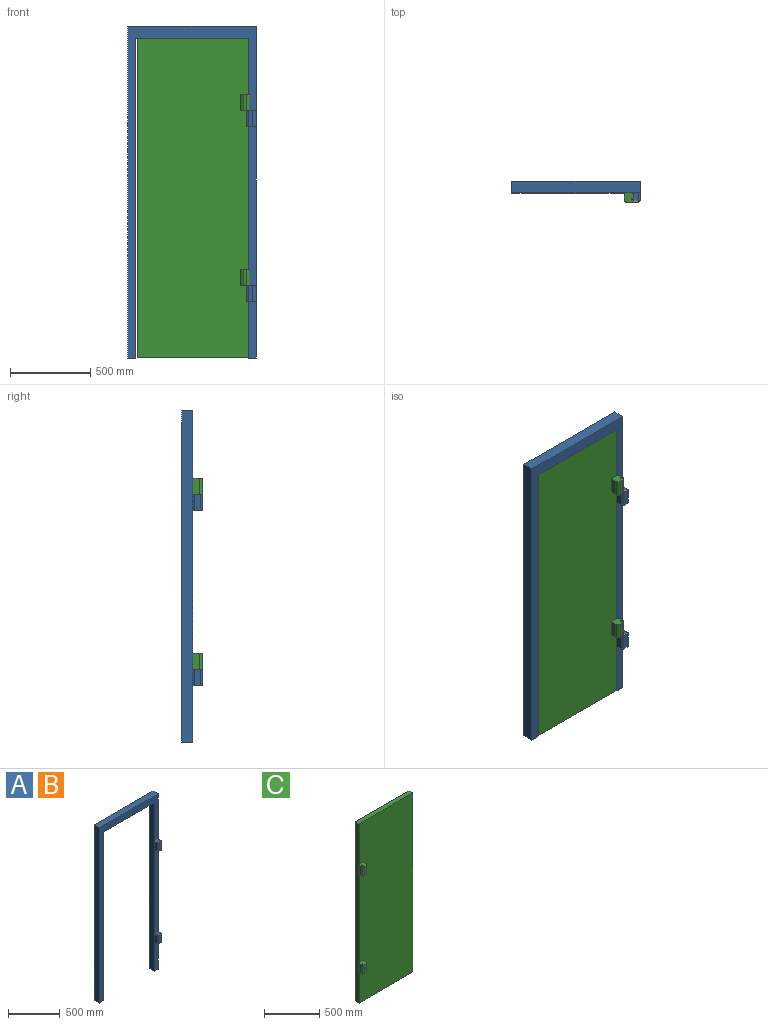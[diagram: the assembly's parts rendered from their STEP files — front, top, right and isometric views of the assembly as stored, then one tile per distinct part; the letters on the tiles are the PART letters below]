
ASSEMBLY  parts=3 mates=1
PART A: 32 faces, bbox 800x130x2070 mm
  f0: plane 2070x800mm, normal (0,-1,0), area 182944.4mm2, adj f2,f3,f4,f5,f6,f7,f9,f16
  f1: plane 1014.1x50mm, normal (0,-1,0), area 49748.1mm2, adj f7,f9,f12,f18,f21,f25
  f2: plane 800x70mm, normal (0,0,1), area 56000mm2, adj f0,f3,f9,f11
  f3: plane 2070x70mm, normal (-1,0,0), area 144900mm2, adj f0,f2,f4,f11
  f4: plane 70x50mm, normal (0,0,-1), area 3500mm2, adj f0,f3,f5,f11
  f5: plane 1994.1x70mm, normal (1,0,0), area 139587.2mm2, adj f0,f4,f6,f11
  f6: plane 700x70mm, normal (0,0,-1), area 49000mm2, adj f0,f5,f7,f11
  f7: plane 1994.1x70mm, normal (-1,0,0), area 139587.2mm2, adj f0,f1,f6,f8,f10,f11,f22,f26
  f8: plane 70x50mm, normal (0,0,-1), area 3500mm2, adj f7,f9,f10,f11
  f9: plane 2070x110mm, normal (1,0,0), area 151300mm2, adj f0,f1,f2,f8,f10,f11,f20,f21
  f10: plane 360x50mm, normal (0,-1,0), area 17521.5mm2, adj f7,f8,f9,f14,f20
  f11: plane 2070x800mm, normal (0,1,0), area 260128.1mm2, adj f2,f3,f4,f5,f6,f7,f8,f9
  f12: plane 60x50mm, normal (0,0,1), area 2869.9mm2, adj f1,f13,f15,f21,f22,f23,f28,f31
  f13: plane 100x40mm, normal (-1,0,0), area 4000mm2, adj f12,f14,f22,f23
  f14: plane 60x50mm, normal (0,0,-1), area 2869.9mm2, adj f10,f13,f15,f20,f22,f23,f28,f31
  f15: plane 100x30mm, normal (0,-1,0), area 3000mm2, adj f12,f14,f23,f28
  f16: plane 60x50mm, normal (0,0,1), area 2869.9mm2, adj f0,f17,f19,f24,f26,f27,f29,f30
  f17: plane 100x40mm, normal (-1,0,0), area 4000mm2, adj f16,f18,f26,f27
  f18: plane 60x50mm, normal (0,0,-1), area 2869.9mm2, adj f1,f17,f19,f25,f26,f27,f29,f30
  f19: plane 100x30mm, normal (0,-1,0), area 3000mm2, adj f16,f18,f27,f29
  f20: cylinder r=10mm len=57.32mm, axis (0,-1,0), area 782.5mm2, adj f9,f10,f14,f28
  f21: cylinder r=10mm len=57.32mm, axis (0,1,0), area 782.5mm2, adj f1,f9,f12,f28
  f22: cylinder r=10mm len=100mm, axis (0,0,-1), area 1570.8mm2, adj f7,f12,f13,f14
  f23: cylinder r=10mm len=100mm, axis (0,0,1), area 1570.8mm2, adj f12,f13,f14,f15
  f24: cylinder r=10mm len=57.32mm, axis (0,1,0), area 782.5mm2, adj f0,f9,f16,f29
  f25: cylinder r=10mm len=57.32mm, axis (0,-1,0), area 782.5mm2, adj f1,f9,f18,f29
  f26: cylinder r=10mm len=100mm, axis (0,0,-1), area 1570.8mm2, adj f7,f16,f17,f18
  f27: cylinder r=10mm len=100mm, axis (0,0,1), area 1570.8mm2, adj f16,f17,f18,f19
  f28: cylinder r=20mm len=100mm, axis (0,0,-1), area 2982.9mm2, adj f9,f12,f14,f15,f20,f21
  f29: cylinder r=20mm len=100mm, axis (0,0,-1), area 2982.9mm2, adj f9,f16,f18,f19,f24,f25
  f30: cylinder r=5mm len=100mm, axis (0,0,1), area 3141.6mm2, adj f16,f18
  f31: cylinder r=5mm len=100mm, axis (0,0,1), area 3141.6mm2, adj f12,f14
PART B: same geometry as A
PART C: 26 faces, bbox 700x110x1990 mm
  f0: plane 1990x690mm, normal (0,-1,0), area 1363104.4mm2, adj f1,f2,f3,f4,f6,f7,f9,f12
  f1: plane 690x50mm, normal (0,0,1), area 34279.6mm2, adj f0,f2,f4,f5
  f2: plane 1990x50mm, normal (-1,0,0), area 99500mm2, adj f0,f1,f3,f5,f20,f23
  f3: plane 690x50mm, normal (0,0,-1), area 34279.6mm2, adj f0,f2,f4,f5
  f4: plane 1990x50mm, normal (0.98,0.17,0), area 101034.9mm2, adj f0,f1,f3,f5
  f5: plane 1990x681.18mm, normal (0,1,0), area 1355555.5mm2, adj f1,f2,f3,f4
  f6: plane 100x40mm, normal (1,0,0), area 4000mm2, adj f0,f7,f9,f24
  f7: plane 60x60mm, normal (0,0,1), area 3299.4mm2, adj f0,f6,f8,f10,f19,f23,f24,f25
  f8: plane 100x22.68mm, normal (-1,0,0), area 2267.9mm2, adj f7,f9,f23,f25
  f9: plane 60x60mm, normal (0,0,-1), area 3299.4mm2, adj f0,f6,f8,f10,f19,f23,f24,f25
  f10: plane 100x20mm, normal (0,-1,0), area 2000mm2, adj f7,f9,f24,f25
  f11: plane 100x22.68mm, normal (-1,0,0), area 2267.9mm2, adj f12,f16,f20,f22
  f12: plane 60x60mm, normal (0,0,-1), area 3299.4mm2, adj f0,f11,f13,f17,f18,f20,f21,f22
  f13: plane 99.89x40mm, normal (1,0,0), area 3995.6mm2, adj f0,f12,f14,f21
  f14: plane 60x40mm, normal (0,0,1), area 2314.2mm2, adj f0,f13,f15,f17,f21
  f15: plane 60x0.11mm, normal (1,0,0), area 6.7mm2, adj f0,f14,f16,f22
  f16: plane 60x20mm, normal (0,0,1), area 985.3mm2, adj f0,f11,f15,f18,f20,f22
  f17: plane 99.89x20mm, normal (0,-1,0), area 1997.8mm2, adj f12,f14,f21,f22
  f18: cylinder r=5mm len=100mm, axis (0,0,-1), area 3141.6mm2, adj f12,f16
  f19: cylinder r=5mm len=100mm, axis (0,0,-1), area 3141.6mm2, adj f7,f9
  f20: cylinder r=20mm len=100mm, axis (0,0,1), area 2094.4mm2, adj f2,f11,f12,f16
  f21: cylinder r=20mm len=99.89mm, axis (0,0,-1), area 3138.1mm2, adj f12,f13,f14,f17
  f22: cylinder r=20mm len=100mm, axis (0,0,1), area 3141.6mm2, adj f11,f12,f15,f16,f17
  f23: cylinder r=20mm len=100mm, axis (0,0,1), area 2094.4mm2, adj f2,f7,f8,f9
  f24: cylinder r=20mm len=100mm, axis (0,0,-1), area 3141.6mm2, adj f6,f7,f9,f10
  f25: cylinder r=20mm len=100mm, axis (0,0,1), area 3141.6mm2, adj f7,f8,f9,f10
PLACE A t=(404.32,293.9,42.54)mm
PLACE B t=(404.32,293.9,42.54)mm
PLACE C rot(axis=(0,1,0),180deg) t=(409.32,273.9,6.64)mm
MATE fastened C.f3 <-> A.f6  axis (0,0,1) through (754.32,223.9,1001.64)mm
